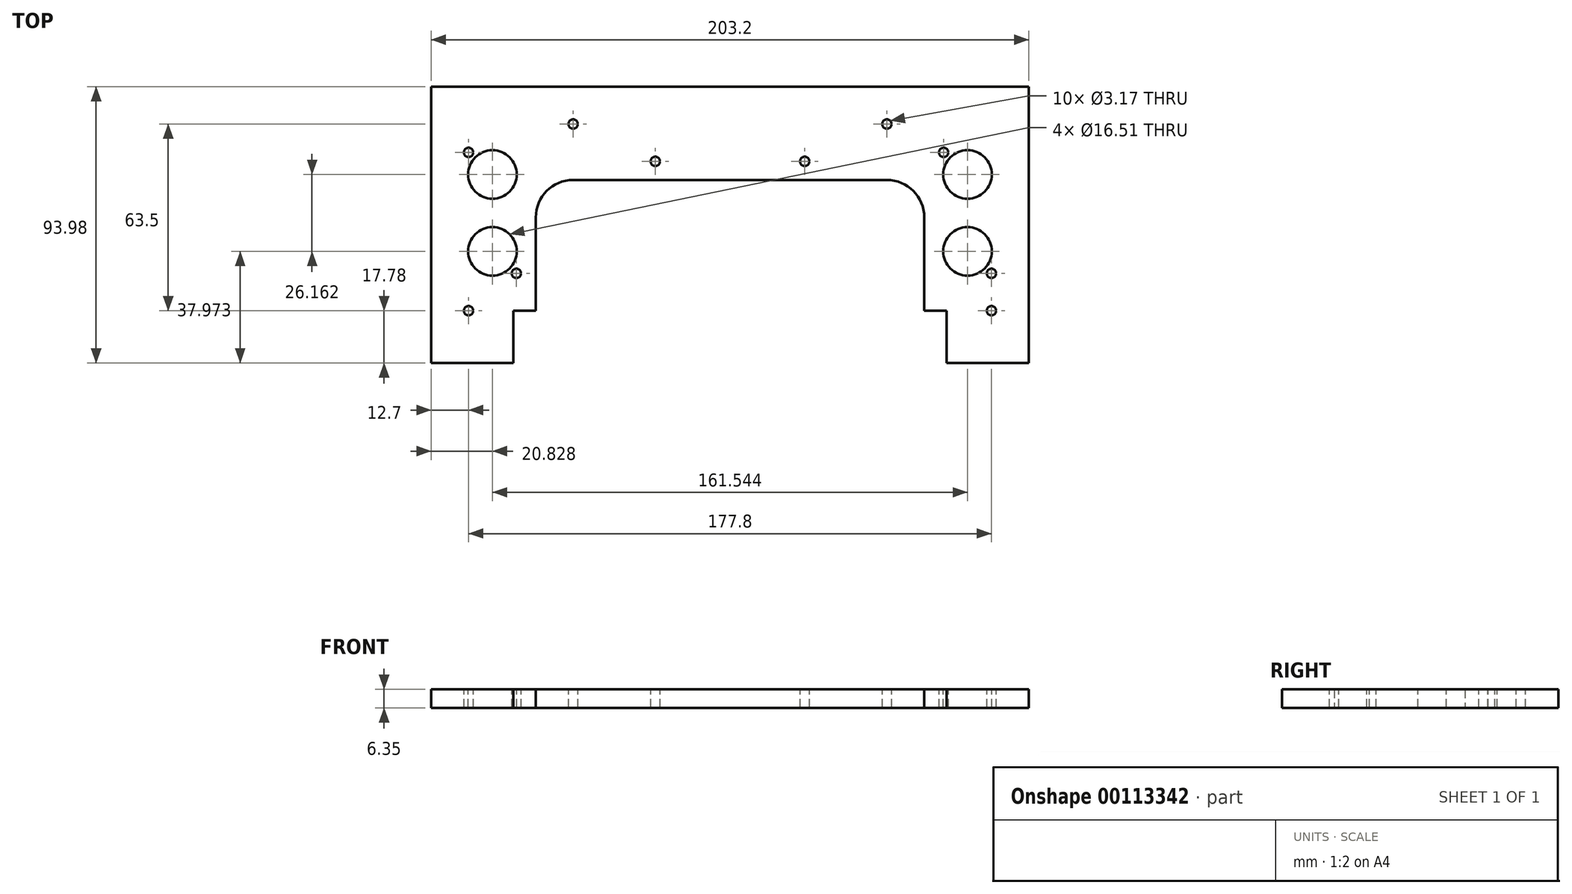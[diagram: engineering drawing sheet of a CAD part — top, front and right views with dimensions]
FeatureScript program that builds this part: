
annotation { "Feature Type Name" : "Feature", "Feature Type Description" : "" }
export const myFeature = defineFeature(function(context is Context, id is Id, definition is map)
    precondition{}
    {
        {
            var Q0;
            Q0=qCreatedBy(makeId("Top.planeOp"),FACE);
            var sketch = newSketch(context, id + "F0", { "sketchPlane" : qUnion([Q0])});
            skLineSegment(sketch, "E0.bottom", {"start": v(0, 0) * mm, "end": v(203.2, 0) * mm});
            skLineSegment(sketch, "E0.top", {"start": v(0, 93.98) * mm, "end": v(203.2, 93.98) * mm});
            skLineSegment(sketch, "E0.left", {"start": v(0, 0) * mm, "end": v(0, 93.98) * mm});
            skLineSegment(sketch, "E0.right", {"start": v(203.2, 0) * mm, "end": v(203.2, 93.98) * mm});
            skLineSegment(sketch, "E1", {"start": v(27.94, 0) * mm, "end": v(27.94, 17.78) * mm});
            skLineSegment(sketch, "E2", {"start": v(27.94, 17.78) * mm, "end": v(35.56, 17.78) * mm});
            skLineSegment(sketch, "E3", {"start": v(35.56, 17.78) * mm, "end": v(35.56, 49.53) * mm});
            skLineSegment(sketch, "E4", {"start": v(48.26, 62.23) * mm, "end": v(154.94, 62.23) * mm});
            skLineSegment(sketch, "E5", {"start": v(167.64, 49.53) * mm, "end": v(167.64, 17.78) * mm});
            skLineSegment(sketch, "E6", {"start": v(167.64, 17.78) * mm, "end": v(175.26, 17.78) * mm});
            skLineSegment(sketch, "E7", {"start": v(175.26, 17.78) * mm, "end": v(175.26, 0) * mm});
            skPoint(sketch, "E8.visualSharp", {"position": v(35.56, 62.23) * mm});
            skArc(sketch, "E8.filletArc", {"start": v(48.26, 62.23) * mm, "mid": v(39.28, 58.51) * mm, "end": v(35.56, 49.53) * mm});
            skPoint(sketch, "E9.visualSharp", {"position": v(167.64, 62.23) * mm});
            skArc(sketch, "E9.filletArc", {"start": v(167.64, 49.53) * mm, "mid": v(163.92, 58.51) * mm, "end": v(154.94, 62.23) * mm});
            skSolve(sketch);
        }
        {
            var Q0;
            Q0=makeQuery(id+"F0.imprint","IMPRINT",FACE,{"disambiguationData":[TD([[makeQuery(id+"F0.imprint","IMPRINT",EDGE,{"derivedFrom":sQuery(id+"F0.wireOp",EDGE,"E0.top")}),-1.0]])]});
            extrude(context, id + "F1", {"entities" : qUnion([Q0]), "depth" : 6.35 * mm});
        }
        {
            var Q0;
            Q0=makeQuery(id+"F1.opExtrude","CAP_FACE",FACE,{"disambiguationData":[OSD([sQuery(id+"F0.wireOp",EDGE,"E0.bottom"),sQuery(id+"F0.wireOp",EDGE,"E0.top"),sQuery(id+"F0.wireOp",EDGE,"E0.left"),sQuery(id+"F0.wireOp",EDGE,"E0.right"),sQuery(id+"F0.wireOp",EDGE,"E1"),sQuery(id+"F0.wireOp",EDGE,"E2"),sQuery(id+"F0.wireOp",EDGE,"E3"),sQuery(id+"F0.wireOp",EDGE,"E4"),sQuery(id+"F0.wireOp",EDGE,"E5"),sQuery(id+"F0.wireOp",EDGE,"E6"),sQuery(id+"F0.wireOp",EDGE,"E7"),sQuery(id+"F0.wireOp",EDGE,"E8.filletArc"),sQuery(id+"F0.wireOp",EDGE,"E9.filletArc")])],"isStart":false});
            var sketch = newSketch(context, id + "F2", { "sketchPlane" : qUnion([Q0])});
            skCircle(sketch, "E10", {"center": v(12.7, 17.78) * mm, "radius": 1.59 * mm});
            skCircle(sketch, "E11", {"center": v(28.96, 30.48) * mm, "radius": 1.59 * mm});
            skCircle(sketch, "E12", {"center": v(20.83, 37.97) * mm, "radius": 8.26 * mm});
            skCircle(sketch, "E13", {"center": v(20.83, 64.13) * mm, "radius": 8.26 * mm});
            skCircle(sketch, "E14", {"center": v(12.7, 71.63) * mm, "radius": 1.59 * mm});
            skCircle(sketch, "E15", {"center": v(48.26, 81.28) * mm, "radius": 1.59 * mm});
            skCircle(sketch, "E16", {"center": v(76.2, 68.58) * mm, "radius": 1.59 * mm});
            skCircle(sketch, "E17", {"center": v(127, 68.58) * mm, "radius": 1.59 * mm});
            skCircle(sketch, "E18", {"center": v(154.94, 81.28) * mm, "radius": 1.59 * mm});
            skCircle(sketch, "E19", {"center": v(174.24, 71.63) * mm, "radius": 1.59 * mm});
            skCircle(sketch, "E20", {"center": v(182.37, 64.14) * mm, "radius": 8.26 * mm});
            skCircle(sketch, "E21", {"center": v(182.37, 37.97) * mm, "radius": 8.26 * mm});
            skCircle(sketch, "E22", {"center": v(190.5, 30.48) * mm, "radius": 1.59 * mm});
            skCircle(sketch, "E23", {"center": v(190.5, 17.78) * mm, "radius": 1.59 * mm});
            skSolve(sketch);
        }
        {
            var Q0;
            Q0 = qSketchRegion(id + "F2", true);
            extrude(context, id + "F3", {"entities" : qUnion([Q0]), "operationType" : NewBodyOperationType.REMOVE, "oppositeDirection" : true, "depth" : 6.35 * mm});
        }
    });
